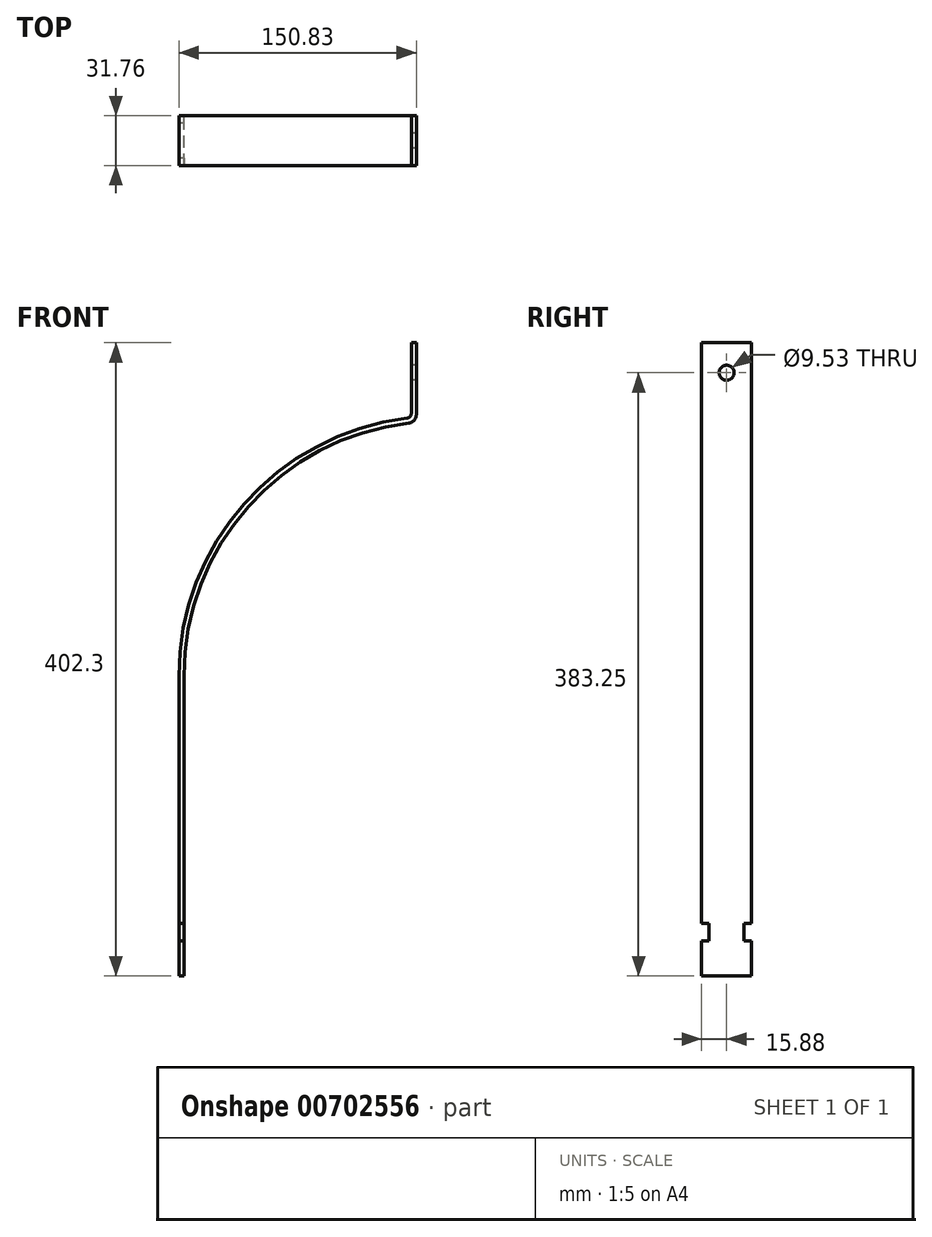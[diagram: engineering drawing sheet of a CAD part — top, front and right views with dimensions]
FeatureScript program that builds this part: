
annotation { "Feature Type Name" : "Feature", "Feature Type Description" : "" }
export const myFeature = defineFeature(function(context is Context, id is Id, definition is map)
    precondition{}
    {
        {
            var Q0;
            Q0=qCreatedBy(makeId("Front.planeOp"),FACE);
            var sketch = newSketch(context, id + "F0", { "sketchPlane" : qUnion([Q0])});
            skArc(sketch, "E0", {"start": v(-12.7, 161.3) * mm, "mid": v(-117.86, 109.34) * mm, "end": v(-160.35, 0) * mm});
            skLineSegment(sketch, "E1", {"start": v(-12.7, 161.3) * mm, "end": v(-12.7, 211.8) * mm});
            skLineSegment(sketch, "E2.0", {"start": v(-15.88, 164.18) * mm, "end": v(-15.88, 211.8) * mm});
            skLineSegment(sketch, "E3", {"start": v(-12.7, 211.8) * mm, "end": v(-15.88, 211.8) * mm});
            skArc(sketch, "E4.0", {"start": v(-15.88, 164.18) * mm, "mid": v(-121.18, 110.4) * mm, "end": v(-163.53, 0) * mm});
            skLineSegment(sketch, "E5", {"start": v(-160.35, 0) * mm, "end": v(-160.35, -190.5) * mm});
            skLineSegment(sketch, "E6.0", {"start": v(-163.53, 0) * mm, "end": v(-163.53, -190.5) * mm});
            skLineSegment(sketch, "E7", {"start": v(81.9, -161.93) * mm, "end": v(-273.7, -161.93) * mm});
            skLineSegment(sketch, "E8", {"start": v(-163.53, -190.5) * mm, "end": v(-160.35, -190.5) * mm});
            skSolve(sketch);
        }
        {
            var Q0;
            Q0 = qSketchRegion(id + "F0", true);
            extrude(context, id + "F1", {"entities" : qUnion([Q0]), "endBound" : BoundingType.SYMMETRIC, "depth" : 31.75 * mm, "offsetDistance" : 25.4 * mm});
        }
        {
            var Q0;
            Q0=makeQuery(id+"F1.opExtrude","SWEPT_EDGE",EDGE,{"disambiguationData":[OSD([sQuery(id+"F0.wireOp",EDGE,"E2.0"),sQuery(id+"F0.wireOp",EDGE,"E4.0")])]});
            fillet(context, id + "F2", {"entities" : qUnion([Q0]), "radius" : 3.17 * mm, "tangentPropagation" : true, "allowEdgeOverflow" : false});
        }
        {
            var Q0;
            Q0=makeQuery(id+"F1.opExtrude","SWEPT_EDGE",EDGE,{"disambiguationData":[OSD([sQuery(id+"F0.wireOp",EDGE,"E0"),sQuery(id+"F0.wireOp",EDGE,"E1")])]});
            fillet(context, id + "F3", {"entities" : qUnion([Q0]), "radius" : 5.08 * mm, "tangentPropagation" : true, "allowEdgeOverflow" : false});
        }
        {
            var Q0;
            Q0=makeQuery(id+"F1.opExtrude","SWEPT_FACE",FACE,{"disambiguationData":[OSD([sQuery(id+"F0.wireOp",EDGE,"E2.0")])]});
            var sketch = newSketch(context, id + "F4", { "sketchPlane" : qUnion([Q0])});
            skCircle(sketch, "E9", {"center": v(0, 192.75) * mm, "radius": 4.76 * mm});
            skSolve(sketch);
        }
        {
            var Q0;
            Q0 = qSketchRegion(id + "F4", true);
            extrude(context, id + "F5", {"entities" : qUnion([Q0]), "operationType" : NewBodyOperationType.REMOVE, "endBound" : BoundingType.THROUGH_ALL, "oppositeDirection" : true, "depth" : 25.4 * mm, "offsetDistance" : 25.4 * mm});
        }
        {
            var Q0;
            Q0=makeQuery(id+"F1.opExtrude","SWEPT_FACE",FACE,{"disambiguationData":[OSD([sQuery(id+"F0.wireOp",EDGE,"E6.0")])]});
            var sketch = newSketch(context, id + "F6", { "sketchPlane" : qUnion([Q0])});
            skLineSegment(sketch, "E10.bottom", {"start": v(-15.88, -168.28) * mm, "end": v(-11.11, -168.28) * mm});
            skLineSegment(sketch, "E10.top", {"start": v(-15.88, -157.16) * mm, "end": v(-11.11, -157.16) * mm});
            skLineSegment(sketch, "E10.left", {"start": v(-15.88, -168.28) * mm, "end": v(-15.88, -157.16) * mm});
            skLineSegment(sketch, "E10.right", {"start": v(-11.11, -168.28) * mm, "end": v(-11.11, -157.16) * mm});
            skLineSegment(sketch, "E11.MirrorCS", {"start": v(11.11, -168.28) * mm, "end": v(11.11, -157.16) * mm});
            skLineSegment(sketch, "E12.MirrorCS", {"start": v(15.88, -157.16) * mm, "end": v(11.11, -157.16) * mm});
            skLineSegment(sketch, "E13.MirrorCS", {"start": v(15.88, -168.28) * mm, "end": v(11.11, -168.28) * mm});
            skLineSegment(sketch, "E14.MirrorCS", {"start": v(15.88, -168.28) * mm, "end": v(15.88, -157.16) * mm});
            skSolve(sketch);
        }
        {
            var Q0;
            Q0 = qSketchRegion(id + "F6", true);
            extrude(context, id + "F7", {"entities" : qUnion([Q0]), "operationType" : NewBodyOperationType.REMOVE, "oppositeDirection" : true, "depth" : 25.4 * mm, "offsetDistance" : 25.4 * mm});
        }
    });
